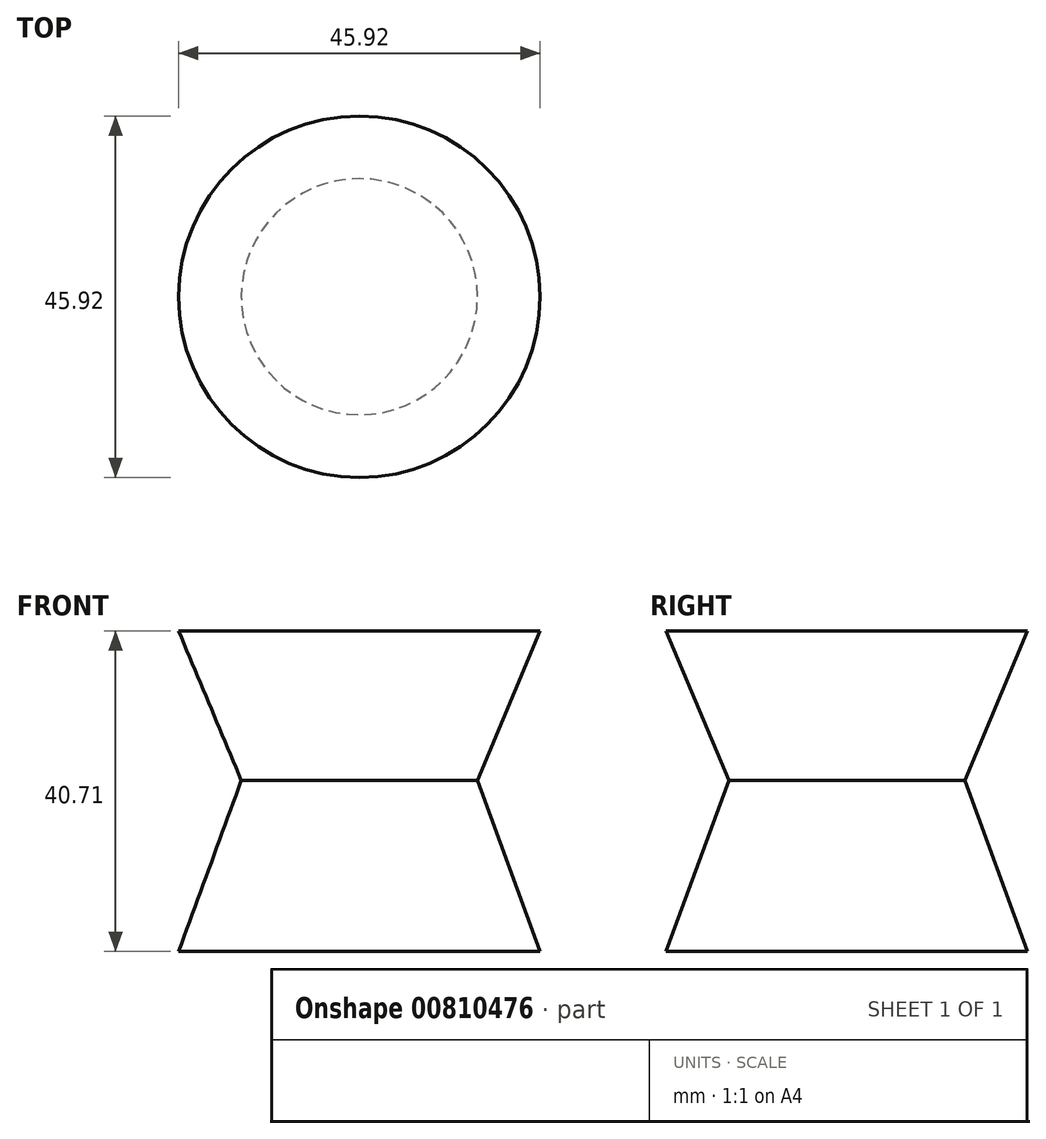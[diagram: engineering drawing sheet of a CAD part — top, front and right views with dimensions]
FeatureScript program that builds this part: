
annotation { "Feature Type Name" : "Feature", "Feature Type Description" : "" }
export const myFeature = defineFeature(function(context is Context, id is Id, definition is map)
    precondition{}
    {
        {
            var Q0;
            Q0=qCreatedBy(makeId("Front.planeOp"),FACE);
            var sketch = newSketch(context, id + "F0", { "sketchPlane" : qUnion([Q0])});
            skLineSegment(sketch, "E0", {"start": v(0, 40.71) * mm, "end": v(22.96, 40.71) * mm});
            skLineSegment(sketch, "E1", {"start": v(22.96, 40.71) * mm, "end": v(15, 21.73) * mm});
            skLineSegment(sketch, "E2", {"start": v(15, 21.73) * mm, "end": v(22.96, 0) * mm});
            skLineSegment(sketch, "E3", {"start": v(22.96, 0) * mm, "end": v(0, 0) * mm});
            skLineSegment(sketch, "E4", {"start": v(0, 0) * mm, "end": v(0, 40.71) * mm});
            skSolve(sketch);
        }
        {
            var Q0;
            Q0=makeQuery(id+"F0.imprint","IMPRINT",FACE,{"disambiguationData":[TD([[makeQuery(id+"F0.imprint","IMPRINT",EDGE,{"derivedFrom":sQuery(id+"F0.wireOp",EDGE,"E0")}),-1.0]])]});
            var Q1;
            Q1=sQuery(id+"F0.wireOp",EDGE,"E4");
            revolve(context, id + "F1", {"surfaceOperationType" : NewSurfaceOperationType.NEW, "entities" : qUnion([Q0]), "axis" : qUnion([Q1]), "revolveType" : RevolveType.FULL});
        }
    });
